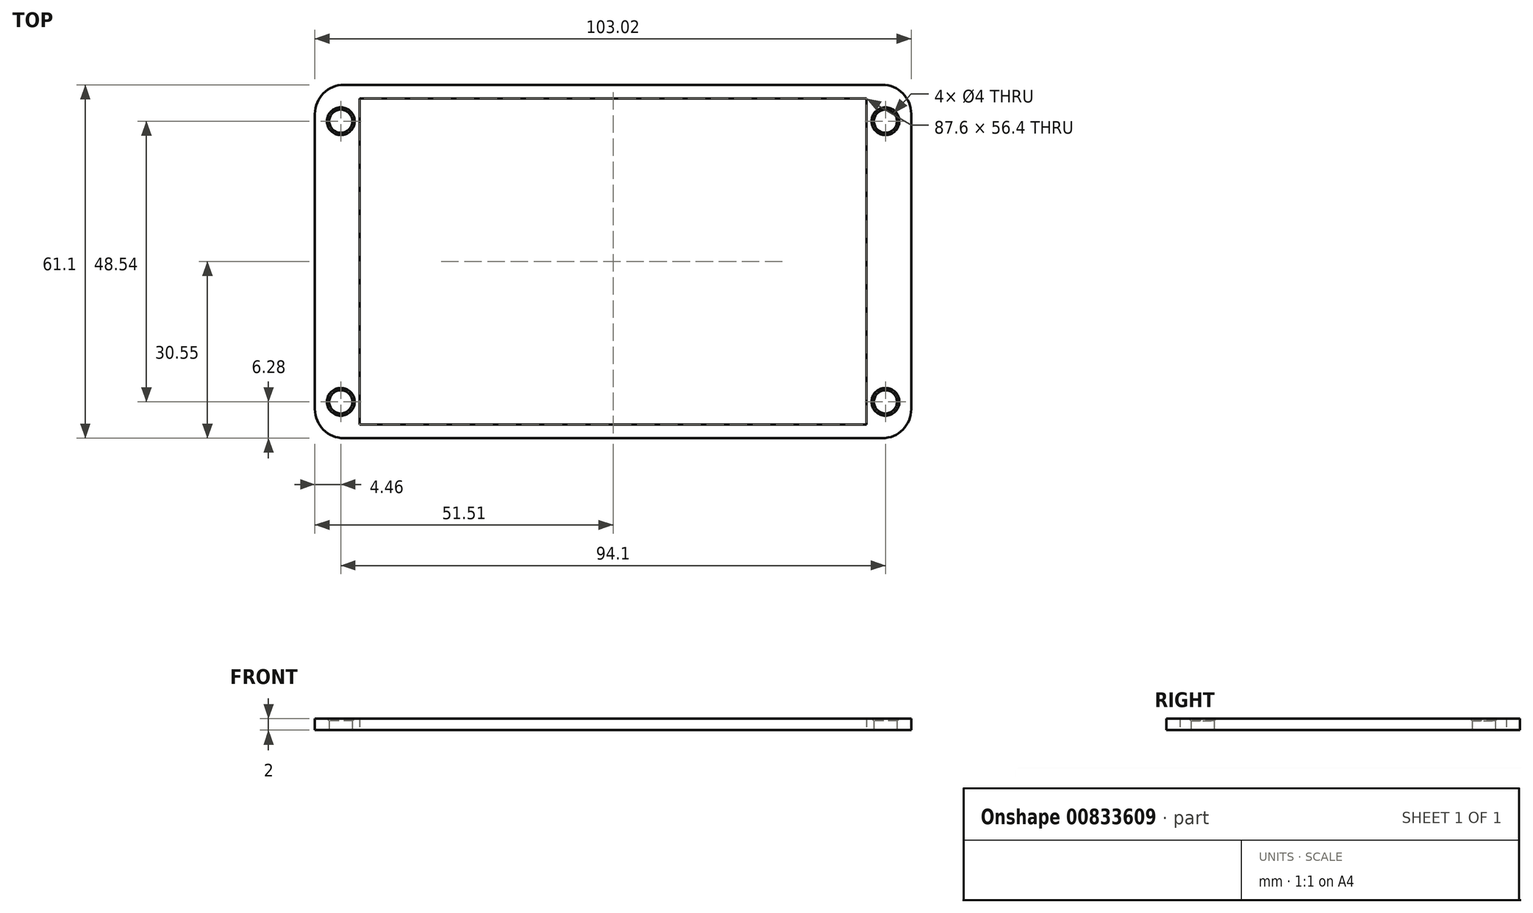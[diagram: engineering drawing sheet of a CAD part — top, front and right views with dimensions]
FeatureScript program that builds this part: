
annotation { "Feature Type Name" : "Feature", "Feature Type Description" : "" }
export const myFeature = defineFeature(function(context is Context, id is Id, definition is map)
    precondition{}
    {
        {
            var Q0;
            Q0=qCreatedBy(makeId("Top.planeOp"),FACE);
            var sketch = newSketch(context, id + "F0", { "sketchPlane" : qUnion([Q0])});
            skLineSegment(sketch, "E0.bottom", {"start": v(-43.8, -28.2) * mm, "end": v(43.8, -28.2) * mm});
            skLineSegment(sketch, "E0.top", {"start": v(-43.8, 28.2) * mm, "end": v(43.8, 28.2) * mm});
            skLineSegment(sketch, "E0.left", {"start": v(-43.8, -28.2) * mm, "end": v(-43.8, 28.2) * mm});
            skLineSegment(sketch, "E0.right", {"start": v(43.8, -28.2) * mm, "end": v(43.8, 28.2) * mm});
            skPoint(sketch, "E0.middle", {"position": v(0, 0) * mm});
            skLineSegment(sketch, "E1.bottom", {"start": v(45.05, -24.27) * mm, "end": v(43.8, -24.27) * mm});
            skCircle(sketch, "E2", {"center": v(47.05, 24.27) * mm, "radius": 2 * mm});
            skCircle(sketch, "E3", {"center": v(47.05, -24.27) * mm, "radius": 2 * mm});
            skCircle(sketch, "E4", {"center": v(-47.05, 24.27) * mm, "radius": 2 * mm});
            skCircle(sketch, "E5", {"center": v(-47.05, -24.27) * mm, "radius": 2 * mm});
            skLineSegment(sketch, "E6.bottom", {"start": v(51.51, 30.55) * mm, "end": v(-51.51, 30.55) * mm});
            skLineSegment(sketch, "E6.top", {"start": v(51.51, -30.55) * mm, "end": v(-51.51, -30.55) * mm});
            skLineSegment(sketch, "E6.left", {"start": v(51.51, 30.55) * mm, "end": v(51.51, -30.55) * mm});
            skLineSegment(sketch, "E6.right", {"start": v(-51.51, 30.55) * mm, "end": v(-51.51, -30.55) * mm});
            skPoint(sketch, "E7.end.orphan", {"position": v(0, 30.55) * mm});
            skPoint(sketch, "E7.start.orphan", {"position": v(0, 28.2) * mm});
            skSolve(sketch);
        }
        {
            var Q0;
            {var subQ3=sQuery(id+"F0.wireOp",EDGE,"E0.bottom");Q0=makeQuery(id+"F0.imprint","IMPRINT",FACE,{"disambiguationData":[TD([[makeQuery(id+"F0.imprint","IMPRINT",EDGE,{"derivedFrom":subQ3}),-1.0]])]});}
            extrude(context, id + "F1", {"entities" : qUnion([Q0]), "depth" : 2 * mm, "offsetDistance" : 25 * mm});
        }
        {
            var Q0;
            Q0=makeQuery(id+"F1.opExtrude","SWEPT_EDGE",EDGE,{"disambiguationData":[OSD([sQuery(id+"F0.wireOp",EDGE,"E6.top"),sQuery(id+"F0.wireOp",EDGE,"E6.left")])]});
            var Q1;
            Q1=makeQuery(id+"F1.opExtrude","SWEPT_EDGE",EDGE,{"disambiguationData":[OSD([sQuery(id+"F0.wireOp",EDGE,"E6.bottom"),sQuery(id+"F0.wireOp",EDGE,"E6.left")])]});
            var Q2;
            Q2=makeQuery(id+"F1.opExtrude","SWEPT_EDGE",EDGE,{"disambiguationData":[OSD([sQuery(id+"F0.wireOp",EDGE,"E6.top"),sQuery(id+"F0.wireOp",EDGE,"E6.right")])]});
            var Q3;
            Q3=makeQuery(id+"F1.opExtrude","SWEPT_EDGE",EDGE,{"disambiguationData":[OSD([sQuery(id+"F0.wireOp",EDGE,"E6.bottom"),sQuery(id+"F0.wireOp",EDGE,"E6.right")])]});
            fillet(context, id + "F2", {"entities" : qUnion([Q0, Q1, Q2, Q3]), "radius" : 5 * mm, "tangentPropagation" : true, "allowEdgeOverflow" : false});
        }
        {
            var Q0;
            Q0=makeQuery(id+"F1.opExtrude","CAP_EDGE",EDGE,{"disambiguationData":[OSD([sQuery(id+"F0.wireOp",EDGE,"E3")])],"isStart":false});
            var Q1;
            Q1=makeQuery(id+"F1.opExtrude","CAP_EDGE",EDGE,{"disambiguationData":[OSD([sQuery(id+"F0.wireOp",EDGE,"E2")])],"isStart":false});
            var Q2;
            Q2=makeQuery(id+"F1.opExtrude","CAP_EDGE",EDGE,{"disambiguationData":[OSD([sQuery(id+"F0.wireOp",EDGE,"E4")])],"isStart":false});
            var Q3;
            Q3=makeQuery(id+"F1.opExtrude","CAP_EDGE",EDGE,{"disambiguationData":[OSD([sQuery(id+"F0.wireOp",EDGE,"E5")])],"isStart":false});
            chamfer(context, id + "F3", {"entities" : qUnion([Q0, Q1, Q2, Q3]), "width" : 0.4 * mm, "tangentPropagation" : true});
        }
    });
